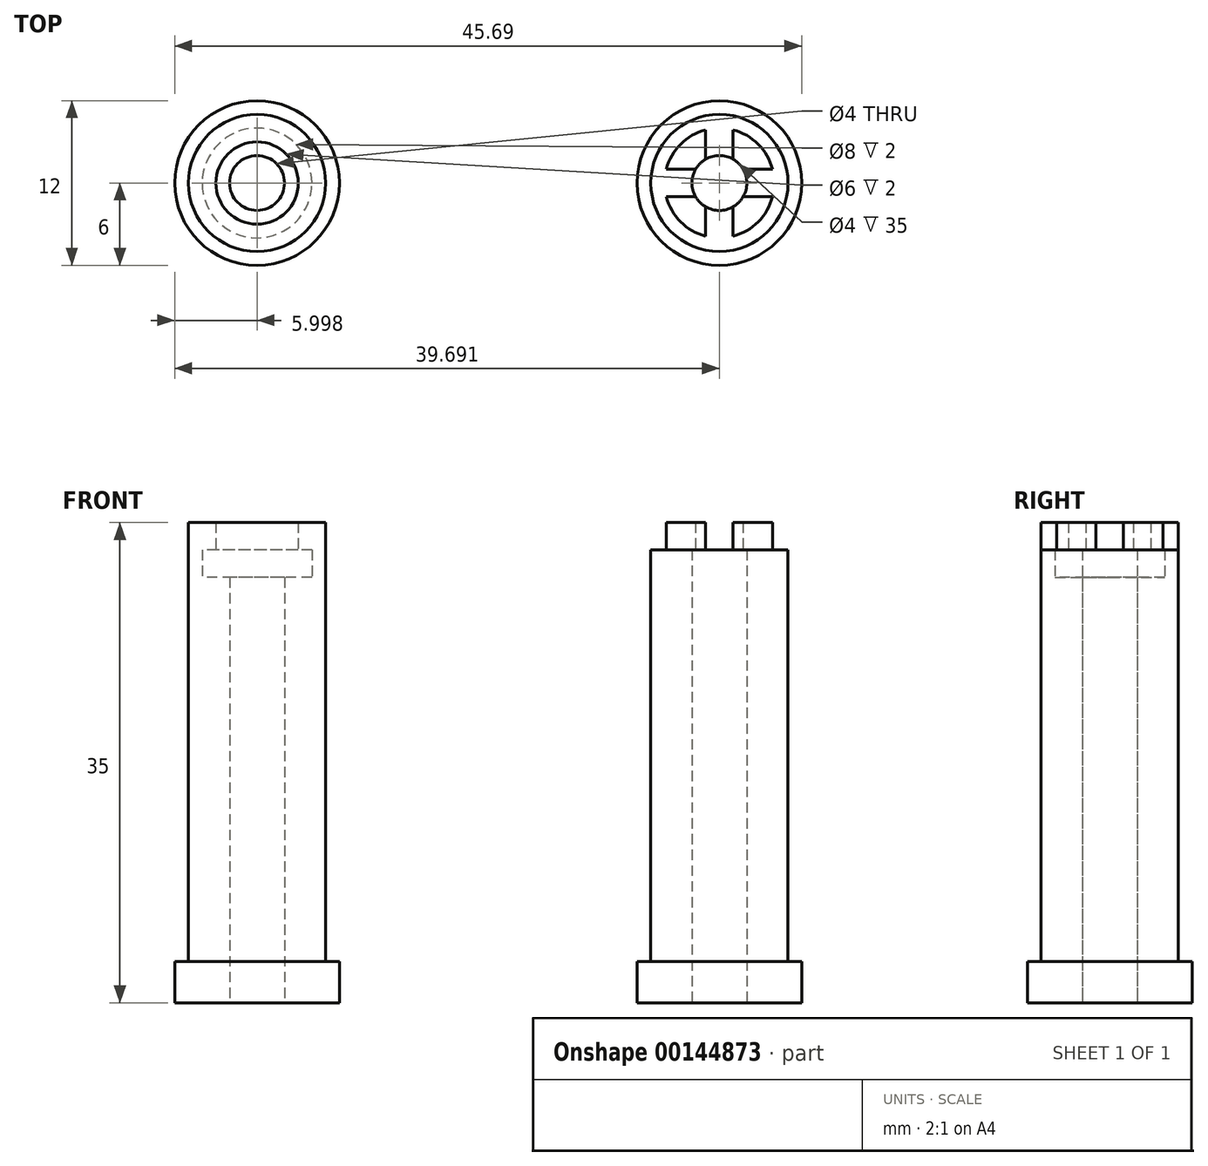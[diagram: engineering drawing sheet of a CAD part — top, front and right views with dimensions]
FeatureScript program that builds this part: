
annotation { "Feature Type Name" : "Feature", "Feature Type Description" : "" }
export const myFeature = defineFeature(function(context is Context, id is Id, definition is map)
    precondition{}
    {
        {
            var Q0;
            Q0=qCreatedBy(makeId("Top.planeOp"),FACE);
            var sketch = newSketch(context, id + "F0", { "sketchPlane" : qUnion([Q0])});
            skCircle(sketch, "E0", {"center": v(-17.02, 0) * mm, "radius": 2 * mm});
            skCircle(sketch, "E1", {"center": v(16.67, 0) * mm, "radius": 2 * mm});
            skCircle(sketch, "E2", {"center": v(-17.02, 0) * mm, "radius": 5 * mm});
            skCircle(sketch, "E3", {"center": v(16.67, 0) * mm, "radius": 5 * mm});
            skCircle(sketch, "E4", {"center": v(-17.02, 0) * mm, "radius": 6 * mm});
            skCircle(sketch, "E5", {"center": v(16.67, 0) * mm, "radius": 6 * mm});
            skSolve(sketch);
        }
        {
            var Q0;
            Q0=makeQuery(id+"F0.imprint","IMPRINT",FACE,{"disambiguationData":[TD([[makeQuery(id+"F0.imprint","IMPRINT",EDGE,{"derivedFrom":sQuery(id+"F0.wireOp",EDGE,"E0")}),-1.0]])]});
            var Q1;
            Q1=makeQuery(id+"F0.imprint","IMPRINT",FACE,{"disambiguationData":[TD([[makeQuery(id+"F0.imprint","IMPRINT",EDGE,{"derivedFrom":sQuery(id+"F0.wireOp",EDGE,"E2")}),-1.0]])]});
            var Q2;
            Q2=makeQuery(id+"F0.imprint","IMPRINT",FACE,{"disambiguationData":[TD([[makeQuery(id+"F0.imprint","IMPRINT",EDGE,{"derivedFrom":sQuery(id+"F0.wireOp",EDGE,"E3")}),-1.0]])]});
            var Q3;
            Q3=makeQuery(id+"F0.imprint","IMPRINT",FACE,{"disambiguationData":[TD([[makeQuery(id+"F0.imprint","IMPRINT",EDGE,{"derivedFrom":sQuery(id+"F0.wireOp",EDGE,"E1")}),-1.0]])]});
            extrude(context, id + "F1", {"entities" : qUnion([Q0, Q1, Q2, Q3]), "depth" : 3 * mm});
        }
        {
            var Q0;
            Q0=makeQuery(id+"F1.opExtrude","CAP_FACE",FACE,{"disambiguationData":[OSD([sQuery(id+"F0.wireOp",EDGE,"E1"),sQuery(id+"F0.wireOp",EDGE,"E5")])],"isStart":false});
            var sketch = newSketch(context, id + "F2", { "sketchPlane" : qUnion([Q0])});
            skCircle(sketch, "E6", {"center": v(16.67, 0) * mm, "radius": 5 * mm});
            skSolve(sketch);
        }
        {
            var Q0;
            Q0=makeQuery(id+"F2.imprint","IMPRINT",FACE,{"disambiguationData":[TD([[makeQuery(id+"F2.imprint","IMPRINT",EDGE,{"derivedFrom":sQuery(id+"F2.wireOp",EDGE,"E6")}),1.0]])]});
            extrude(context, id + "F3", {"entities" : qUnion([Q0]), "operationType" : NewBodyOperationType.ADD, "depth" : 28 * mm});
        }
        {
            var Q0;
            Q0=makeQuery(id+"F3.opExtrude","CAP_FACE",FACE,{"disambiguationData":[OSD([sQuery(id+"F0.wireOp",EDGE,"E1"),sQuery(id+"F2.wireOp",EDGE,"E6")])],"isStart":false});
            var sketch = newSketch(context, id + "F4", { "sketchPlane" : qUnion([Q0])});
            skCircle(sketch, "E7", {"center": v(16.67, 0) * mm, "radius": 3 * mm});
            skSolve(sketch);
        }
        {
            var Q0;
            Q0=makeQuery(id+"F4.imprint","IMPRINT",FACE,{"disambiguationData":[TD([[makeQuery(id+"F4.imprint","IMPRINT",EDGE,{"derivedFrom":sQuery(id+"F4.wireOp",EDGE,"E7")}),1.0]])]});
            extrude(context, id + "F5", {"entities" : qUnion([Q0]), "operationType" : NewBodyOperationType.ADD, "depth" : 2 * mm});
        }
        {
            var Q0;
            Q0=makeQuery(id+"F5.opExtrude","CAP_FACE",FACE,{"disambiguationData":[OSD([sQuery(id+"F0.wireOp",EDGE,"E1"),sQuery(id+"F4.wireOp",EDGE,"E7")])],"isStart":false});
            var sketch = newSketch(context, id + "F6", { "sketchPlane" : qUnion([Q0])});
            skCircle(sketch, "E8", {"center": v(16.67, 0) * mm, "radius": 4 * mm});
            skSolve(sketch);
        }
        {
            var Q0;
            Q0=makeQuery(id+"F6.imprint","IMPRINT",FACE,{"disambiguationData":[TD([[makeQuery(id+"F6.imprint","IMPRINT",EDGE,{"derivedFrom":makeQuery(id+"F5.opExtrude","CAP_EDGE",EDGE,{"disambiguationData":[OSD([sQuery(id+"F4.wireOp",EDGE,"E7")])],"isStart":false})}),1.0]])]});
            var Q1;
            Q1=makeQuery(id+"F6.imprint","IMPRINT",FACE,{"disambiguationData":[TD([[makeQuery(id+"F6.imprint","IMPRINT",EDGE,{"derivedFrom":sQuery(id+"F6.wireOp",EDGE,"E8")}),1.0]])]});
            extrude(context, id + "F7", {"entities" : qUnion([Q0, Q1]), "operationType" : NewBodyOperationType.ADD, "depth" : 2 * mm});
        }
        {
            var Q0;
            Q0=makeQuery(id+"F7.opExtrude","CAP_FACE",FACE,{"disambiguationData":[OSD([sQuery(id+"F0.wireOp",EDGE,"E1"),sQuery(id+"F6.wireOp",EDGE,"E8")])],"isStart":false});
            var sketch = newSketch(context, id + "F8", { "sketchPlane" : qUnion([Q0])});
            skLineSegment(sketch, "E9", {"start": v(17.67, -4) * mm, "end": v(17.67, 4) * mm});
            skLineSegment(sketch, "E10", {"start": v(17.67, 4) * mm, "end": v(15.67, 4) * mm});
            skLineSegment(sketch, "E11", {"start": v(15.67, 4) * mm, "end": v(15.67, -4) * mm});
            skLineSegment(sketch, "E12", {"start": v(15.67, -4) * mm, "end": v(17.67, -4) * mm});
            skLineSegment(sketch, "E13", {"start": v(12.67, 1) * mm, "end": v(20.67, 1) * mm});
            skLineSegment(sketch, "E14", {"start": v(20.67, 1) * mm, "end": v(20.67, -1) * mm});
            skLineSegment(sketch, "E15", {"start": v(20.67, -1) * mm, "end": v(12.67, -1) * mm});
            skLineSegment(sketch, "E16", {"start": v(12.67, -1) * mm, "end": v(12.67, 1) * mm});
            skSolve(sketch);
        }
        {
            var Q0;
            Q0 = qSketchRegion(id + "F8", true);
            extrude(context, id + "F9", {"entities" : qUnion([Q0]), "operationType" : NewBodyOperationType.REMOVE, "oppositeDirection" : true, "depth" : 4 * mm});
        }
        {
            var Q0;
            Q0=makeQuery(id+"F1.opExtrude","CAP_FACE",FACE,{"disambiguationData":[OSD([sQuery(id+"F0.wireOp",EDGE,"E0"),sQuery(id+"F0.wireOp",EDGE,"E4")])],"isStart":false});
            var sketch = newSketch(context, id + "F10", { "sketchPlane" : qUnion([Q0])});
            skCircle(sketch, "E17", {"center": v(-17.02, 0) * mm, "radius": 5 * mm});
            skSolve(sketch);
        }
        {
            var Q0;
            Q0=makeQuery(id+"F10.imprint","IMPRINT",FACE,{"disambiguationData":[TD([[makeQuery(id+"F10.imprint","IMPRINT",EDGE,{"derivedFrom":sQuery(id+"F10.wireOp",EDGE,"E17")}),1.0]])]});
            extrude(context, id + "F11", {"entities" : qUnion([Q0]), "operationType" : NewBodyOperationType.ADD, "depth" : 28 * mm});
        }
        {
            var Q0;
            Q0=makeQuery(id+"F11.opExtrude","CAP_FACE",FACE,{"disambiguationData":[OSD([sQuery(id+"F0.wireOp",EDGE,"E0"),sQuery(id+"F10.wireOp",EDGE,"E17")])],"isStart":false});
            var sketch = newSketch(context, id + "F12", { "sketchPlane" : qUnion([Q0])});
            skCircle(sketch, "E18", {"center": v(-17.02, 0) * mm, "radius": 4 * mm});
            skSolve(sketch);
        }
        {
            var Q0;
            Q0=makeQuery(id+"F12.imprint","IMPRINT",FACE,{"disambiguationData":[TD([[makeQuery(id+"F12.imprint","IMPRINT",EDGE,{"derivedFrom":sQuery(id+"F12.wireOp",EDGE,"E18")}),-1.0]])]});
            extrude(context, id + "F13", {"entities" : qUnion([Q0]), "operationType" : NewBodyOperationType.ADD, "depth" : 2 * mm});
        }
        {
            var Q0;
            Q0=makeQuery(id+"F13.opExtrude","CAP_FACE",FACE,{"disambiguationData":[OSD([sQuery(id+"F10.wireOp",EDGE,"E17"),sQuery(id+"F12.wireOp",EDGE,"E18")])],"isStart":false});
            var sketch = newSketch(context, id + "F14", { "sketchPlane" : qUnion([Q0])});
            skCircle(sketch, "E19", {"center": v(-17.02, 0) * mm, "radius": 3 * mm});
            skSolve(sketch);
        }
        {
            var Q0;
            Q0=makeQuery(id+"F14.imprint","IMPRINT",FACE,{"disambiguationData":[TD([[makeQuery(id+"F14.imprint","IMPRINT",EDGE,{"derivedFrom":sQuery(id+"F14.wireOp",EDGE,"E19")}),-1.0]])]});
            var Q1;
            Q1=makeQuery(id+"F14.imprint","IMPRINT",FACE,{"disambiguationData":[TD([[makeQuery(id+"F14.imprint","IMPRINT",EDGE,{"derivedFrom":makeQuery(id+"F13.opExtrude","CAP_EDGE",EDGE,{"disambiguationData":[OSD([sQuery(id+"F12.wireOp",EDGE,"E18")])],"isStart":false})}),-1.0]])]});
            var Q2;
            Q2=makeQuery(id+"F9.boolean.opBoolean","MERGE",FACE,{"derivedFrom":[makeQuery(id+"F3.opExtrude","CAP_FACE",FACE,{"disambiguationData":[OSD([sQuery(id+"F0.wireOp",EDGE,"E1"),sQuery(id+"F2.wireOp",EDGE,"E6")])],"isStart":false}),makeQuery(id+"F9.opExtrude","CAP_FACE",FACE,{"disambiguationData":[OSD([sQuery(id+"F8.wireOp",EDGE,"E9"),sQuery(id+"F8.wireOp",EDGE,"E10"),sQuery(id+"F8.wireOp",EDGE,"E11"),sQuery(id+"F8.wireOp",EDGE,"E12"),sQuery(id+"F8.wireOp",EDGE,"E13"),sQuery(id+"F8.wireOp",EDGE,"E14"),sQuery(id+"F8.wireOp",EDGE,"E15"),sQuery(id+"F8.wireOp",EDGE,"E16")])],"isStart":false})]});
            extrude(context, id + "F15", {"entities" : qUnion([Q0, Q1, Q2]), "operationType" : NewBodyOperationType.ADD, "depth" : 2 * mm});
        }
    });
